# Revit family: Считыватель AGRG AXI 2_тип модель
name_source: partatom
category: Охранная сигнализация
units: mm (PartAtom-declared; Revit-internal decimal feet)

## family parameters
Всегда вертикально = Да
На основе рабочей плоскости = Нет
Общий = Нет
При загрузке вырезать с полостями = Нет
Размер круглого соединителя = Использовать диаметр
Сохранять ориентацию аннотаций = Нет
Тип детали = Нормальный
Точка расчета площади = Нет

## types (3) — shared parameters
ADSK_Верхний порог напряжения = 15 В
ADSK_Группирование = 1. Оборудование
ADSK_Единица измерения = шт.
ADSK_Завод-изготовитель = ООО «Агрегатор»
ADSK_Количество = 1
ADSK_Марка = AGRG AXI
ADSK_Масса = 0.06
ADSK_Наименование краткое = Считыватель бесконтактных карт
ADSK_Нижний порог напряжения = 9 В
ADSK_Обозначение = RC
ITV_SUB_УГО на структурной схеме = УГО_Считыватель
URL = https://skud.agrg.ru
Изображение типоразмера = RC.png
Описание = ITV
Стоимость = 14250 $

## per-type parameters (varying)
| type | ADSK_Код изделия | ADSK_Наименование | Материал |
| Считыватель AGRG AXI 2 «Арктический белый» | AXI2AW | Считыватель для СКУД AGRG AXI 2 "Арктический белый"; Форматы карт: MIFARE (UID);Mifare Mini, Mifare Classic, Mifare Plus SL1/SL3, Mifare DESFire (UID и чтение из защищенной области);Mifare ID (UID и чтение из защищенной области, только рабочие карты);I-CODE (ISO15693) (UID);EM-Marine (UID);HID 125 кГц (UID);Indala (Motorola) (UID) Размер, мм: 82х38х10; IP54; -40 … +50 гр. Материал корпуса: искусственный камень на базе акрила. | Пластмасса, непрозрачная, белая |
| Считыватель AGRG AXI 2 «Люксовый Мандарин» | AXI2LM | Считыватель для СКУД AGRG AXI 2 "Люксовый мандарин"; Форматы карт: MIFARE (UID);Mifare Mini, Mifare Classic, Mifare Plus SL1/SL3, Mifare DESFire (UID и чтение из защищенной области);Mifare ID (UID и чтение из защищенной области, только рабочие карты);I-CODE (ISO15693) (UID);EM-Marine (UID);HID 125 кГц (UID);Indala (Motorola) (UID) Размер, мм: 82х38х10; IP54; -40 … +50 гр. Материал корпуса: искусственный камень на базе акрила. | Пластмасса, непрозрачная, оранжевая |
| Считыватель AGRG AXI 2 «Имперский черный» | AXI2IBL | Считыватель для СКУД AGRG AXI 2 "Имперский черный"; Форматы карт: MIFARE (UID);Mifare Mini, Mifare Classic, Mifare Plus SL1/SL3, Mifare DESFire (UID и чтение из защищенной области);Mifare ID (UID и чтение из защищенной области, только рабочие карты);I-CODE (ISO15693) (UID);EM-Marine (UID);HID 125 кГц (UID);Indala (Motorola) (UID) Размер, мм: 82х38х10; IP54; -40 … +50 гр. Материал корпуса: искусственный камень на базе акрила. | Пластмасса, непрозрачная, черная |
